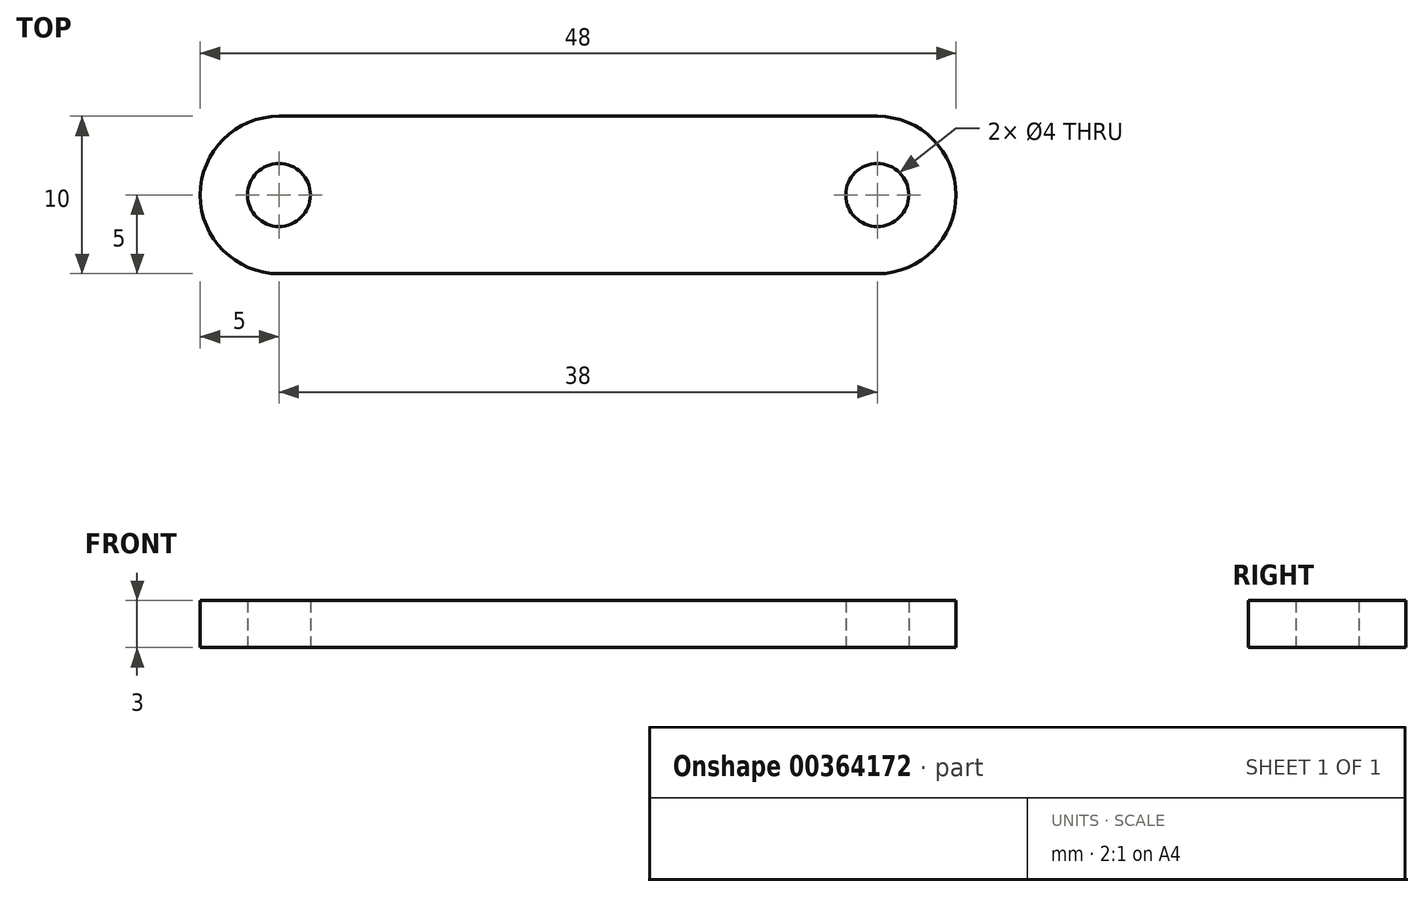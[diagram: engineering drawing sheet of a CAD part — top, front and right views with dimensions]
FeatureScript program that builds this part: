
annotation { "Feature Type Name" : "Feature", "Feature Type Description" : "" }
export const myFeature = defineFeature(function(context is Context, id is Id, definition is map)
    precondition{}
    {
        {
            var Q0;
            Q0=qCreatedBy(makeId("Top.planeOp"),FACE);
            var sketch = newSketch(context, id + "F0", { "sketchPlane" : qUnion([Q0])});
            skLineSegment(sketch, "E0.bottom", {"start": v(19, 5) * mm, "end": v(-19, 5) * mm});
            skLineSegment(sketch, "E0.top", {"start": v(19, -5) * mm, "end": v(-19, -5) * mm});
            skPoint(sketch, "E0.middle", {"position": v(0, 0) * mm});
            skCircle(sketch, "E1", {"center": v(-19, 0) * mm, "radius": 2 * mm});
            skCircle(sketch, "E2", {"center": v(19, 0) * mm, "radius": 2 * mm});
            skArc(sketch, "E3", {"start": v(-19, 5) * mm, "mid": v(-24, 0) * mm, "end": v(-19, -5) * mm});
            skArc(sketch, "E4", {"start": v(19, -5) * mm, "mid": v(24, 0) * mm, "end": v(19, 5) * mm});
            skSolve(sketch);
        }
        {
            var Q0;
            Q0 = qSketchRegion(id + "F0", true);
            extrude(context, id + "F1", {"entities" : qUnion([Q0]), "depth" : 3 * mm});
        }
    });
